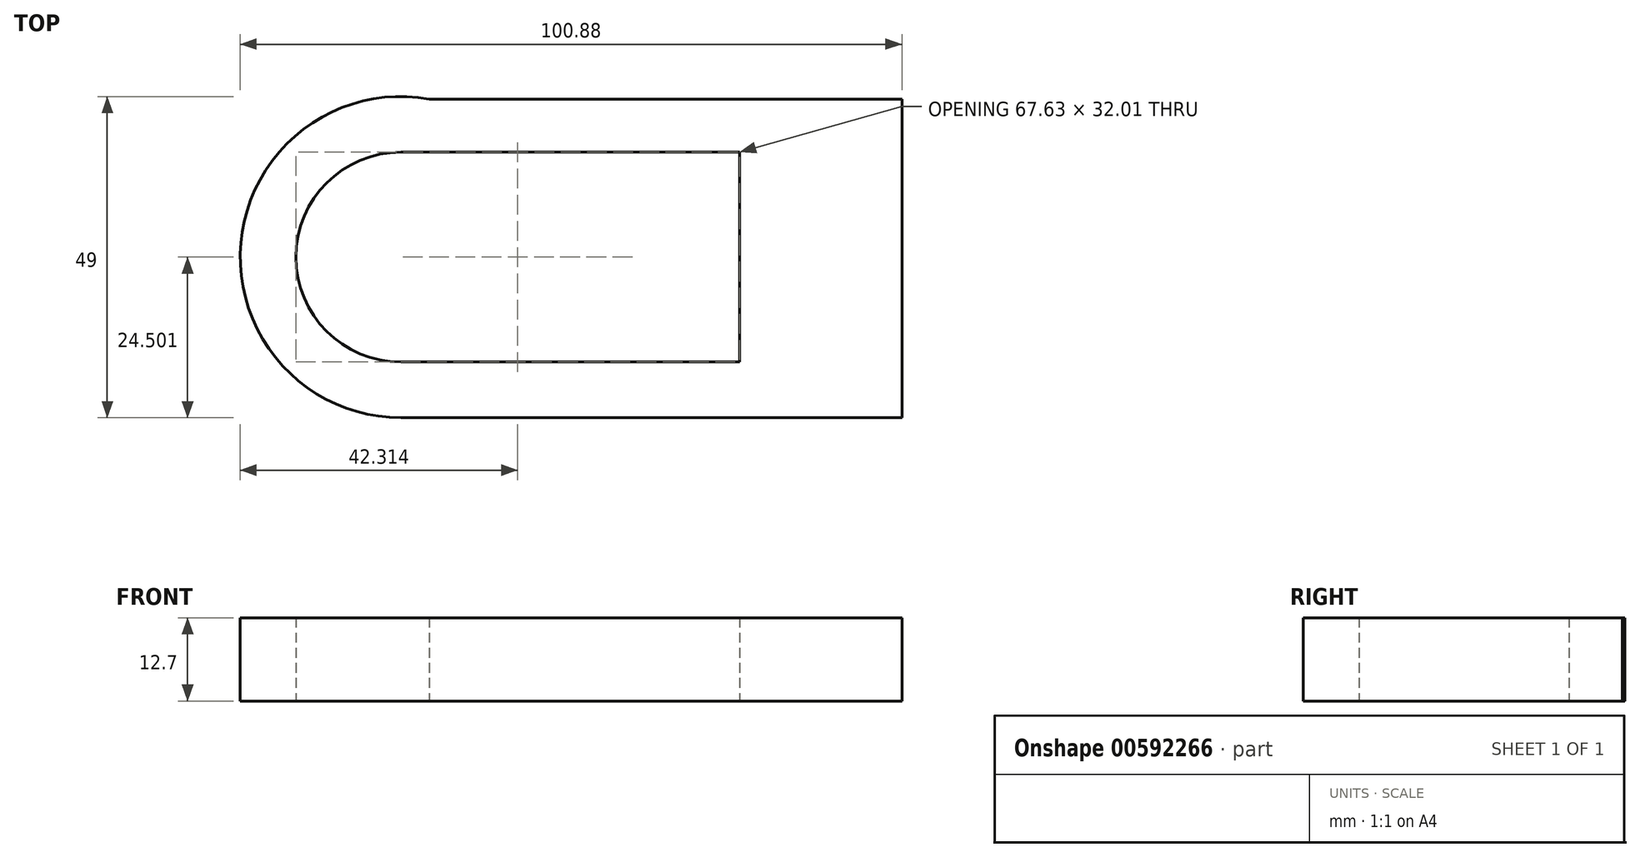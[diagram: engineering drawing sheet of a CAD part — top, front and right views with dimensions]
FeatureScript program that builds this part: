
annotation { "Feature Type Name" : "Feature", "Feature Type Description" : "" }
export const myFeature = defineFeature(function(context is Context, id is Id, definition is map)
    precondition{}
    {
        {
            var Q0;
            Q0=qCreatedBy(makeId("Top.planeOp"),FACE);
            var sketch = newSketch(context, id + "F0", { "sketchPlane" : qUnion([Q0])});
            skLineSegment(sketch, "E0.bottom", {"start": v(-51.63, -25.51) * mm, "end": v(24.75, -25.51) * mm});
            skLineSegment(sketch, "E0.top", {"start": v(-51.63, 23.1) * mm, "end": v(24.75, 23.1) * mm});
            skLineSegment(sketch, "E0.left", {"start": v(-51.63, -25.51) * mm, "end": v(-51.63, 23.1) * mm});
            skLineSegment(sketch, "E0.right", {"start": v(24.75, -25.51) * mm, "end": v(24.75, 23.1) * mm});
            skLineSegment(sketch, "E1.bottom", {"start": v(0, -17.01) * mm, "end": v(-51.63, -17.01) * mm});
            skLineSegment(sketch, "E1.top", {"start": v(0, 15) * mm, "end": v(-51.63, 15) * mm});
            skLineSegment(sketch, "E1.left", {"start": v(0, -17.01) * mm, "end": v(0, 15) * mm});
            skLineSegment(sketch, "E1.right", {"start": v(-51.63, -17.01) * mm, "end": v(-51.63, 15) * mm});
            skCircle(sketch, "E2", {"center": v(-51.63, -1) * mm, "radius": 24.5 * mm});
            skCircle(sketch, "E3", {"center": v(-51.63, -1) * mm, "radius": 16 * mm});
            skSolve(sketch);
        }
        {
            var Q0;
            {var subQ0=sQuery(id+"F0.wireOp",EDGE,"E0.left");var subQ1=sQuery(id+"F0.wireOp",EDGE,"E0.top");var subQ2=makeQuery(id+"F0.imprint","INTERSECT",VERTEX,{"derivedFrom":[subQ1,subQ0]});Q0=makeQuery(id+"F0.imprint","IMPRINT",FACE,{"disambiguationData":[TD([[makeQuery(id+"F0.imprint","IMPRINT",EDGE,{"disambiguationData":[TD([[subQ2,-1.0]])],"derivedFrom":subQ1}),1.0]])]});}
            var Q1;
            {var subQ7=sQuery(id+"F0.wireOp",EDGE,"E0.bottom");Q1=makeQuery(id+"F0.imprint","IMPRINT",FACE,{"disambiguationData":[TD([[makeQuery(id+"F0.imprint","IMPRINT",EDGE,{"derivedFrom":subQ7}),1.0]])]});}
            var Q2;
            {var subQ0=sQuery(id+"F0.wireOp",EDGE,"E2");var subQ3=sQuery(id+"F0.wireOp",EDGE,"E1.bottom");var subQ5=makeQuery(id+"F0.imprint","INTERSECT",VERTEX,{"derivedFrom":[subQ3,subQ0]});Q2=makeQuery(id+"F0.imprint","IMPRINT",FACE,{"disambiguationData":[TD([[makeQuery(id+"F0.imprint","IMPRINT",EDGE,{"disambiguationData":[TD([[subQ5,1.0]])],"derivedFrom":subQ0}),1.0]])]});}
            var Q3;
            {var subQ0=sQuery(id+"F0.wireOp",EDGE,"E0.left");var subQ1=sQuery(id+"F0.wireOp",EDGE,"E0.top");var subQ2=makeQuery(id+"F0.imprint","INTERSECT",VERTEX,{"derivedFrom":[subQ1,subQ0]});Q3=makeQuery(id+"F0.imprint","IMPRINT",FACE,{"disambiguationData":[TD([[makeQuery(id+"F0.imprint","IMPRINT",EDGE,{"disambiguationData":[TD([[subQ2,-1.0]])],"derivedFrom":subQ1}),-1.0]])]});}
            extrude(context, id + "F1", {"entities" : qUnion([Q0, Q1, Q2, Q3]), "depth" : 12.7 * mm, "offsetDistance" : 25.4 * mm});
        }
    });
